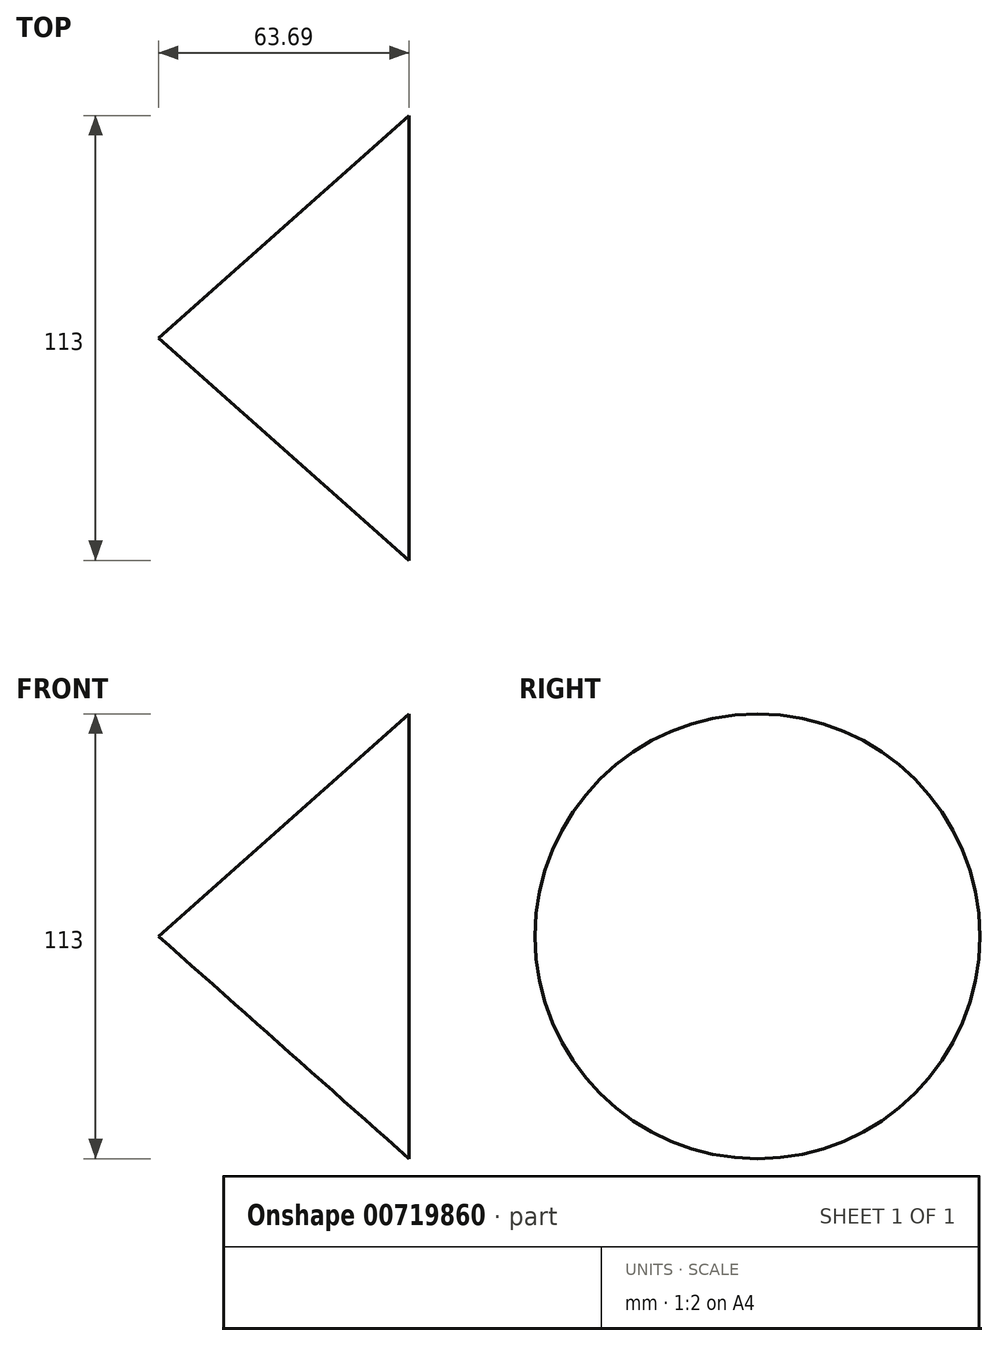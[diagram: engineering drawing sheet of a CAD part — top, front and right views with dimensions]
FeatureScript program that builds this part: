
annotation { "Feature Type Name" : "Feature", "Feature Type Description" : "" }
export const myFeature = defineFeature(function(context is Context, id is Id, definition is map)
    precondition{}
    {
        {
            var Q0;
            Q0=qCreatedBy(makeId("Front.planeOp"),FACE);
            var sketch = newSketch(context, id + "F0", { "sketchPlane" : qUnion([Q0])});
            skLineSegment(sketch, "E0", {"start": v(0, 56.5) * mm, "end": v(-63.7, 0) * mm});
            skLineSegment(sketch, "E1", {"start": v(-63.7, 0) * mm, "end": v(0, 0) * mm});
            skSolve(sketch);
        }
        {
            var Q0;
            Q0=sQuery(id+"F0.wireOp",EDGE,"E0");
            var Q1;
            Q1=sQuery(id+"F0.wireOp",EDGE,"E1");
            revolve(context, id + "F1", {"bodyType" : ToolBodyType.SURFACE, "surfaceOperationType" : NewSurfaceOperationType.NEW, "surfaceEntities" : qUnion([Q0]), "axis" : qUnion([Q1]), "revolveType" : RevolveType.FULL});
        }
    });
